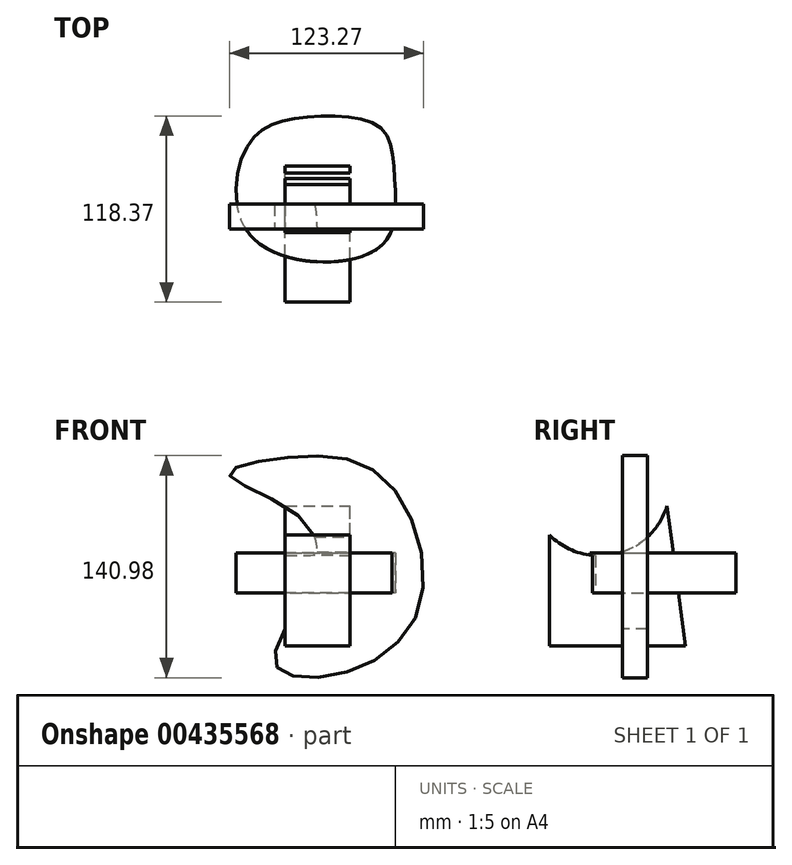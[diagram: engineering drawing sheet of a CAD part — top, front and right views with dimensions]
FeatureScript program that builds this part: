
annotation { "Feature Type Name" : "Feature", "Feature Type Description" : "" }
export const myFeature = defineFeature(function(context is Context, id is Id, definition is map)
    precondition{}
    {
        {
            var Q0;
            Q0=qCreatedBy(makeId("Front.planeOp"),FACE);
            var sketch = newSketch(context, id + "F0", { "sketchPlane" : qUnion([Q0])});
            skFitSpline(sketch, "E0", {"points": [v(-76.49, 74.99) * mm, v(-29.25, 45.9) * mm, v(-28.5, 0) * mm, v(-47.54, -45.3) * mm, v(-9.45, -52.04) * mm, v(43.94, -9.15) * mm, v(21, 73.34) * mm, v(-45.14, 85.49) * mm, v(-76.49, 74.99) * mm]});
            skSolve(sketch);
        }
        {
            var Q0;
            Q0=makeQuery(id+"F0.imprint","IMPRINT",FACE,{"disambiguationData":[TD([[makeQuery(id+"F0.imprint","IMPRINT",EDGE,{"derivedFrom":sQuery(id+"F0.wireOp",EDGE,"E0")}),1.0]])]});
            var sketch = newSketch(context, id + "F1", { "sketchPlane" : qUnion([Q0])});
            skSolve(sketch);
        }
        {
            var Q0;
            Q0=makeQuery(id+"F1.imprint","IMPRINT",FACE,{"disambiguationData":[TD([[makeQuery(id+"F1.imprint","IMPRINT",EDGE,{"derivedFrom":makeQuery(id+"F0.imprint","IMPRINT",EDGE,{"derivedFrom":sQuery(id+"F0.wireOp",EDGE,"E0")})}),1.0]])]});
            extrude(context, id + "F2", {"entities" : qUnion([Q0]), "oppositeDirection" : true, "depth" : 15.92 * mm});
        }
        {
            var Q0;
            Q0=qCreatedBy(makeId("Top.planeOp"),FACE);
            var sketch = newSketch(context, id + "F3", { "sketchPlane" : qUnion([Q0])});
            skFitSpline(sketch, "E1", {"points": [v(-61.25, -6) * mm, v(-64.48, 53.98) * mm, v(-28.8, 71.2) * mm, v(19.18, 64.44) * mm, v(28.26, 31.84) * mm, v(18.26, -11.69) * mm, v(-61.25, -6) * mm]});
            skSolve(sketch);
        }
        {
            var Q0;
            Q0=makeQuery(id+"F3.imprint","IMPRINT",FACE,{"disambiguationData":[TD([[makeQuery(id+"F3.imprint","IMPRINT",EDGE,{"derivedFrom":sQuery(id+"F3.wireOp",EDGE,"E1")}),-1.0]])]});
            extrude(context, id + "F4", {"entities" : qUnion([Q0]), "operationType" : NewBodyOperationType.ADD, "depth" : 25.4 * mm});
        }
        {
            var Q0;
            Q0=qCreatedBy(makeId("Right.planeOp"),FACE);
            var sketch = newSketch(context, id + "F5", { "sketchPlane" : qUnion([Q0])});
            skArc(sketch, "E2", {"start": v(-46.33, 36.71) * mm, "mid": v(-3.83, 24.93) * mm, "end": v(28.25, 55.2) * mm});
            skLineSegment(sketch, "E3", {"start": v(-46.33, -33.58) * mm, "end": v(40.07, -33.58) * mm});
            skLineSegment(sketch, "E4", {"start": v(40.07, -33.58) * mm, "end": v(28.25, 55.2) * mm});
            skLineSegment(sketch, "E5", {"start": v(-46.33, 36.71) * mm, "end": v(-46.33, -33.58) * mm});
            skSolve(sketch);
        }
        {
            var Q0;
            Q0=makeQuery(id+"F5.imprint","IMPRINT",FACE,{"disambiguationData":[TD([[makeQuery(id+"F5.imprint","IMPRINT",EDGE,{"derivedFrom":sQuery(id+"F5.wireOp",EDGE,"E2")}),-1.0]])]});
            extrude(context, id + "F6", {"entities" : qUnion([Q0]), "operationType" : NewBodyOperationType.ADD, "oppositeDirection" : true, "depth" : 41.2 * mm});
        }
    });
